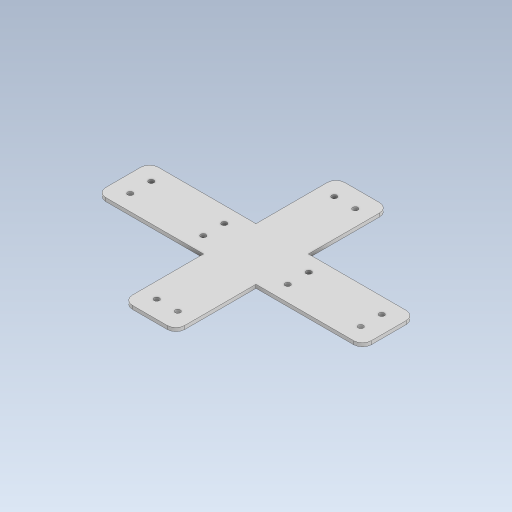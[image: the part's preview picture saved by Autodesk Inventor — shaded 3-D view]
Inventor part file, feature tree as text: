
AUTODESK INVENTOR PART (.ipt)
format: ipt  version: 2023.5 (Build 275446000, 446)  size: 332,288 bytes
history: native  units: in
note: dims shown in document units (in); Inventor stores cm internally (conversion verified against a paired STEP export)
features: extrude x1, sketch x1
ambient origin geometry x8: Origin, YZ Plane, XZ Plane, XY Plane, X Axis, Y Axis, Z Axis, Center Point
bodies: Solid1 (feature_tree)
feature tree (2):
  extrude  "Extrusion1"  Depth=0.0787in
  sketch  "Sketch1"  dims[d1=0.9498in d3=0.2362in d4=0.1181in d5=1.6437in d6=0.1181in d7=1.998in d8=0.2362in d9=0.5906in d10=0.3937in d11=0.5906in d12=0.3937in d13=0.1969in d14=0.1969in d15=0.0787in d16=0.0in]
